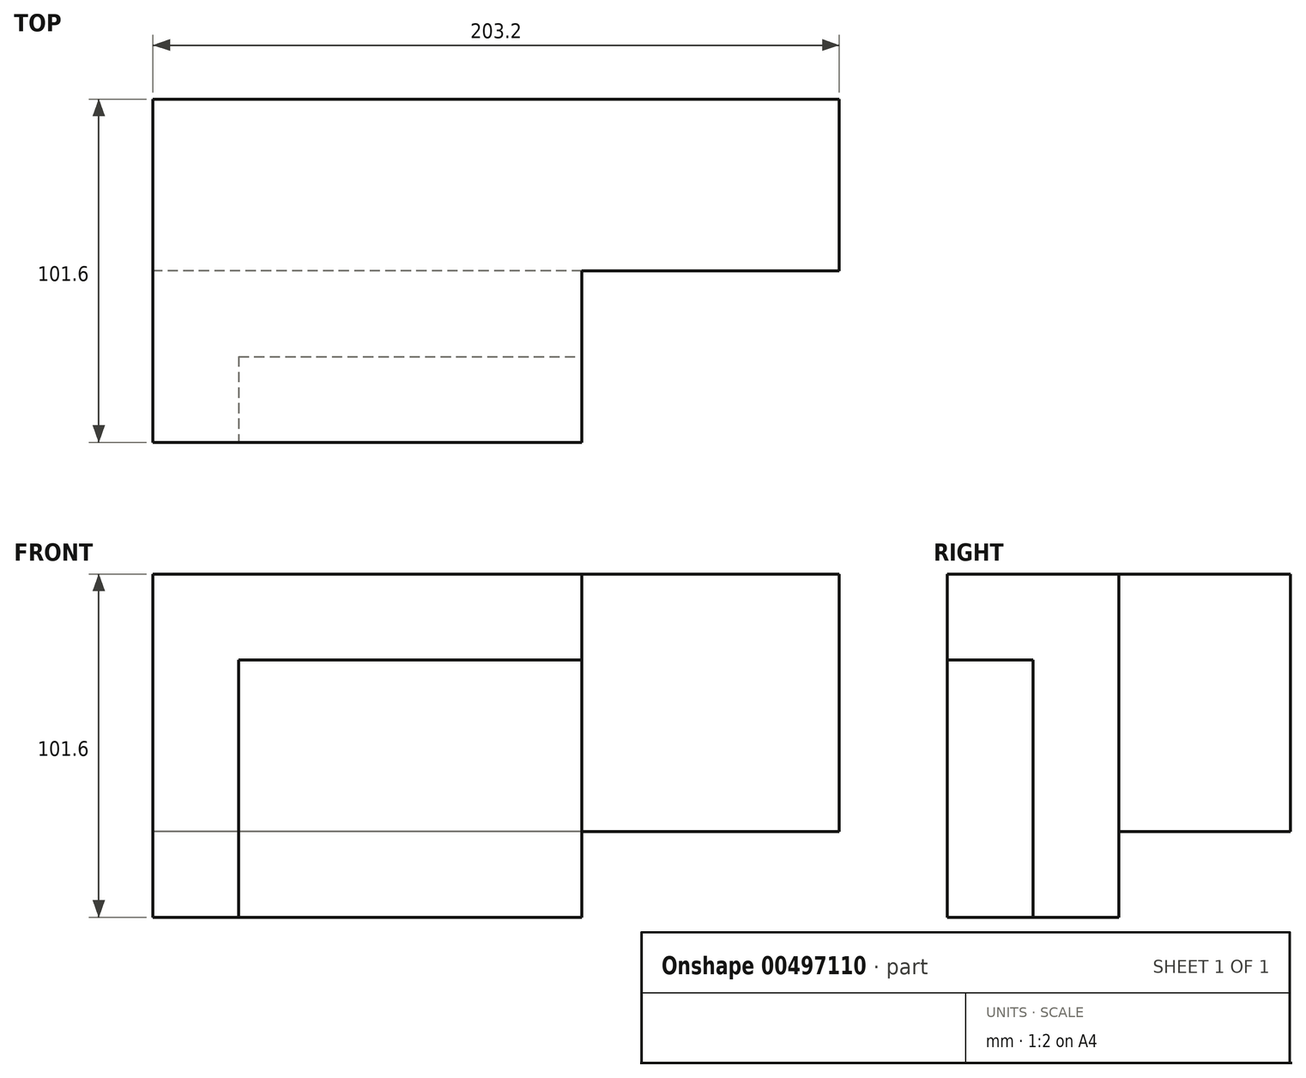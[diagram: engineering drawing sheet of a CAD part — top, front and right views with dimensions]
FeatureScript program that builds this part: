
annotation { "Feature Type Name" : "Feature", "Feature Type Description" : "" }
export const myFeature = defineFeature(function(context is Context, id is Id, definition is map)
    precondition{}
    {
        {
            var Q0;
            Q0=qCreatedBy(makeId("Front.planeOp"),FACE);
            var sketch = newSketch(context, id + "F0", { "sketchPlane" : qUnion([Q0])});
            skLineSegment(sketch, "E0.bottom", {"start": v(0, 0) * mm, "end": v(-203.2, 0) * mm});
            skLineSegment(sketch, "E0.top", {"start": v(0, 76.2) * mm, "end": v(-203.2, 76.2) * mm});
            skLineSegment(sketch, "E0.left", {"start": v(0, 0) * mm, "end": v(0, 76.2) * mm});
            skLineSegment(sketch, "E0.right", {"start": v(-203.2, 0) * mm, "end": v(-203.2, 76.2) * mm});
            skSolve(sketch);
        }
        {
            var Q0;
            Q0=makeQuery(id+"F0.imprint","IMPRINT",FACE,{"disambiguationData":[TD([[makeQuery(id+"F0.imprint","IMPRINT",EDGE,{"derivedFrom":sQuery(id+"F0.wireOp",EDGE,"E0.bottom")}),-1.0]])]});
            extrude(context, id + "F1", {"entities" : qUnion([Q0]), "depth" : 50.8 * mm});
        }
        {
            var Q0;
            Q0=makeQuery(id+"F1.opExtrude","CAP_FACE",FACE,{"disambiguationData":[OSD([sQuery(id+"F0.wireOp",EDGE,"E0.bottom"),sQuery(id+"F0.wireOp",EDGE,"E0.top"),sQuery(id+"F0.wireOp",EDGE,"E0.left"),sQuery(id+"F0.wireOp",EDGE,"E0.right")])],"isStart":false});
            var sketch = newSketch(context, id + "F2", { "sketchPlane" : qUnion([Q0])});
            skLineSegment(sketch, "E1.bottom", {"start": v(-203.2, 76.2) * mm, "end": v(-76.2, 76.2) * mm});
            skLineSegment(sketch, "E1.top", {"start": v(-203.2, -25.4) * mm, "end": v(-76.2, -25.4) * mm});
            skLineSegment(sketch, "E1.left", {"start": v(-203.2, 76.2) * mm, "end": v(-203.2, -25.4) * mm});
            skLineSegment(sketch, "E1.right", {"start": v(-76.2, 76.2) * mm, "end": v(-76.2, -25.4) * mm});
            skSolve(sketch);
        }
        {
            var Q0;
            {var subQ0=sQuery(id+"F2.wireOp",EDGE,"E1.bottom");Q0=makeQuery(id+"F2.imprint","IMPRINT",FACE,{"disambiguationData":[TD([[makeQuery(id+"F2.imprint","IMPRINT",EDGE,{"derivedFrom":subQ0}),1.0]])]});}
            var Q1;
            {var subQ0=sQuery(id+"F2.wireOp",EDGE,"E1.top");Q1=makeQuery(id+"F2.imprint","IMPRINT",FACE,{"disambiguationData":[TD([[makeQuery(id+"F2.imprint","IMPRINT",EDGE,{"derivedFrom":subQ0}),1.0]])]});}
            extrude(context, id + "F3", {"entities" : qUnion([Q0, Q1]), "operationType" : NewBodyOperationType.ADD, "depth" : 50.8 * mm});
        }
        {
            var Q0;
            Q0=makeQuery(id+"F3.opExtrude","CAP_FACE",FACE,{"disambiguationData":[OSD([sQuery(id+"F2.wireOp",EDGE,"E1.bottom"),sQuery(id+"F2.wireOp",EDGE,"E1.top"),sQuery(id+"F2.wireOp",EDGE,"E1.left"),sQuery(id+"F2.wireOp",EDGE,"E1.right")])],"isStart":false});
            var sketch = newSketch(context, id + "F4", { "sketchPlane" : qUnion([Q0])});
            skLineSegment(sketch, "E2.bottom", {"start": v(-76.2, -25.4) * mm, "end": v(-177.8, -25.4) * mm});
            skLineSegment(sketch, "E2.top", {"start": v(-76.2, 50.8) * mm, "end": v(-177.8, 50.8) * mm});
            skLineSegment(sketch, "E2.left", {"start": v(-76.2, -25.4) * mm, "end": v(-76.2, 50.8) * mm});
            skLineSegment(sketch, "E2.right", {"start": v(-177.8, -25.4) * mm, "end": v(-177.8, 50.8) * mm});
            skSolve(sketch);
        }
        {
            var Q0;
            Q0=makeQuery(id+"F4.imprint","IMPRINT",FACE,{"disambiguationData":[TD([[makeQuery(id+"F4.imprint","IMPRINT",EDGE,{"derivedFrom":sQuery(id+"F4.wireOp",EDGE,"E2.bottom")}),1.0]])]});
            extrude(context, id + "F5", {"entities" : qUnion([Q0]), "operationType" : NewBodyOperationType.REMOVE, "oppositeDirection" : true, "depth" : 25.4 * mm});
        }
    });
